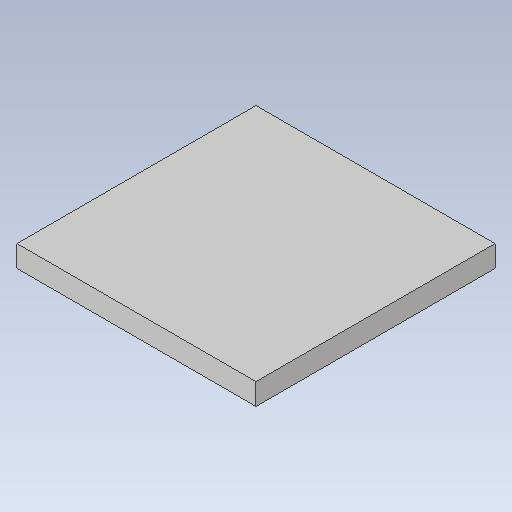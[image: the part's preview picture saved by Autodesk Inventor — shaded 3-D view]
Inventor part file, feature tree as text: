
AUTODESK INVENTOR PART (.ipt)
format: ipt  version: 2020 (Build 240168000, 168)  size: 92,160 bytes
history: native  units: mm
features: other x1, extrude x1, sketch x1
ambient origin geometry x8: Origin, YZ Plane, XZ Plane, XY Plane, X Axis, Y Axis, Z Axis, Center Point
bodies: Body1 (feature_tree)
feature tree (3):
  other  "Bryła1"
  extrude  "Wyciągnięcie proste1"  Depth=40.0mm
  sketch  "Szkic1"
